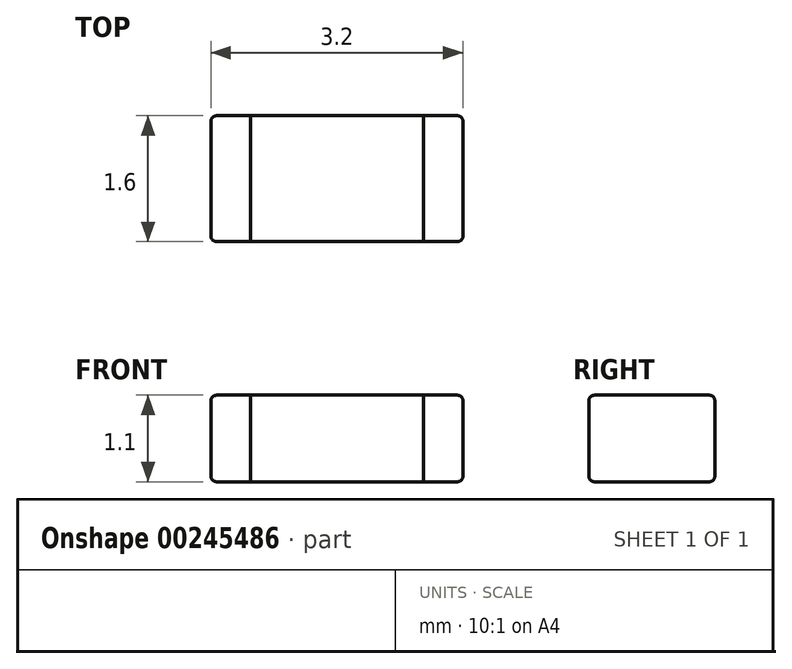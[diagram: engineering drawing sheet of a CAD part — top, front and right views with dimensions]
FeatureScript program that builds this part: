
annotation { "Feature Type Name" : "Feature", "Feature Type Description" : "" }
export const myFeature = defineFeature(function(context is Context, id is Id, definition is map)
    precondition{}
    {
        {
            var Q0;
            Q0=qCreatedBy(makeId("Top.planeOp"),FACE);
            var sketch = newSketch(context, id + "F0", { "sketchPlane" : qUnion([Q0])});
            skLineSegment(sketch, "E0.bottom", {"start": v(1.6, -0.8) * mm, "end": v(-1.6, -0.8) * mm});
            skLineSegment(sketch, "E0.top", {"start": v(1.6, 0.8) * mm, "end": v(-1.6, 0.8) * mm});
            skLineSegment(sketch, "E0.left", {"start": v(1.6, -0.8) * mm, "end": v(1.6, 0.8) * mm});
            skLineSegment(sketch, "E0.right", {"start": v(-1.6, -0.8) * mm, "end": v(-1.6, 0.8) * mm});
            skPoint(sketch, "E0.middle", {"position": v(0, 0) * mm});
            skLineSegment(sketch, "E1", {"start": v(-1.1, 0.8) * mm, "end": v(-1.1, -0.8) * mm});
            skLineSegment(sketch, "E2", {"start": v(1.1, 0.8) * mm, "end": v(1.1, -0.8) * mm});
            skSolve(sketch);
        }
        {
            var Q0;
            {var subQ0=sQuery(id+"F0.wireOp",EDGE,"E0.right");Q0=makeQuery(id+"F0.imprint","IMPRINT",FACE,{"disambiguationData":[TD([[makeQuery(id+"F0.imprint","IMPRINT",EDGE,{"derivedFrom":subQ0}),-1.0]])]});}
            var Q1;
            {var subQ0=sQuery(id+"F0.wireOp",EDGE,"E0.left");Q1=makeQuery(id+"F0.imprint","IMPRINT",FACE,{"disambiguationData":[TD([[makeQuery(id+"F0.imprint","IMPRINT",EDGE,{"derivedFrom":subQ0}),1.0]])]});}
            extrude(context, id + "F1", {"entities" : qUnion([Q0, Q1]), "depth" : 1.1 * mm});
        }
        {
            var Q0;
            {var subQ0=sQuery(id+"F0.wireOp",EDGE,"E1");Q0=makeQuery(id+"F0.imprint","IMPRINT",FACE,{"disambiguationData":[TD([[makeQuery(id+"F0.imprint","IMPRINT",EDGE,{"derivedFrom":subQ0}),1.0]])]});}
            extrude(context, id + "F2", {"entities" : qUnion([Q0]), "depth" : 1.1 * mm});
        }
        {
            var Q0;
            Q0=makeQuery(id+"F1.opExtrude","SWEPT_FACE",FACE,{"disambiguationData":[OSD([sQuery(id+"F0.wireOp",EDGE,"E0.left")])]});
            var Q1;
            Q1=makeQuery(id+"F1.opExtrude","SWEPT_FACE",FACE,{"disambiguationData":[OSD([sQuery(id+"F0.wireOp",EDGE,"E0.right")])]});
            fillet(context, id + "F3", {"entities" : qUnion([Q0, Q1]), "radius" : 0.07 * mm, "tangentPropagation" : true, "allowEdgeOverflow" : false});
        }
        {
            var Q0;
            {var subQ0=sQuery(id+"F0.wireOp",EDGE,"E0.top");Q0=makeQuery(id+"F1.opExtrude","CAP_EDGE",EDGE,{"disambiguationData":[OSD([subQ0]),TDD([makeQuery(id+"F0.imprint","IMPRINT",EDGE,{"disambiguationData":[TD([[makeQuery(id+"F0.imprint","INTERSECT",VERTEX,{"derivedFrom":[subQ0,sQuery(id+"F0.wireOp",EDGE,"E0.left")]}),-1.0]])],"derivedFrom":subQ0})])],"isStart":false});}
            var Q1;
            Q1=makeQuery(id+"F2.opExtrude","CAP_EDGE",EDGE,{"disambiguationData":[OSD([sQuery(id+"F0.wireOp",EDGE,"E0.top")])],"isStart":false});
            var Q2;
            {var subQ0=sQuery(id+"F0.wireOp",EDGE,"E0.top");Q2=makeQuery(id+"F1.opExtrude","CAP_EDGE",EDGE,{"disambiguationData":[OSD([subQ0]),TDD([makeQuery(id+"F0.imprint","IMPRINT",EDGE,{"disambiguationData":[TD([[makeQuery(id+"F0.imprint","INTERSECT",VERTEX,{"derivedFrom":[subQ0,sQuery(id+"F0.wireOp",EDGE,"E0.right")]}),1.0]])],"derivedFrom":subQ0})])],"isStart":false});}
            var Q3;
            Q3=makeQuery(id+"F2.opExtrude","CAP_EDGE",EDGE,{"disambiguationData":[OSD([sQuery(id+"F0.wireOp",EDGE,"E0.top")])],"isStart":true});
            var Q4;
            {var subQ0=sQuery(id+"F0.wireOp",EDGE,"E0.top");Q4=makeQuery(id+"F1.opExtrude","CAP_EDGE",EDGE,{"disambiguationData":[OSD([subQ0]),TDD([makeQuery(id+"F0.imprint","IMPRINT",EDGE,{"disambiguationData":[TD([[makeQuery(id+"F0.imprint","INTERSECT",VERTEX,{"derivedFrom":[subQ0,sQuery(id+"F0.wireOp",EDGE,"E0.right")]}),1.0]])],"derivedFrom":subQ0})])],"isStart":true});}
            var Q5;
            {var subQ0=sQuery(id+"F0.wireOp",EDGE,"E0.top");Q5=makeQuery(id+"F1.opExtrude","CAP_EDGE",EDGE,{"disambiguationData":[OSD([subQ0]),TDD([makeQuery(id+"F0.imprint","IMPRINT",EDGE,{"disambiguationData":[TD([[makeQuery(id+"F0.imprint","INTERSECT",VERTEX,{"derivedFrom":[subQ0,sQuery(id+"F0.wireOp",EDGE,"E0.left")]}),-1.0]])],"derivedFrom":subQ0})])],"isStart":true});}
            var Q6;
            {var subQ0=sQuery(id+"F0.wireOp",EDGE,"E0.bottom");Q6=makeQuery(id+"F1.opExtrude","CAP_EDGE",EDGE,{"disambiguationData":[OSD([subQ0]),TDD([makeQuery(id+"F0.imprint","IMPRINT",EDGE,{"disambiguationData":[TD([[makeQuery(id+"F0.imprint","INTERSECT",VERTEX,{"derivedFrom":[subQ0,sQuery(id+"F0.wireOp",EDGE,"E0.left")]}),-1.0]])],"derivedFrom":subQ0})])],"isStart":false});}
            var Q7;
            Q7=makeQuery(id+"F2.opExtrude","CAP_EDGE",EDGE,{"disambiguationData":[OSD([sQuery(id+"F0.wireOp",EDGE,"E0.bottom")])],"isStart":false});
            var Q8;
            {var subQ0=sQuery(id+"F0.wireOp",EDGE,"E0.bottom");Q8=makeQuery(id+"F1.opExtrude","CAP_EDGE",EDGE,{"disambiguationData":[OSD([subQ0]),TDD([makeQuery(id+"F0.imprint","IMPRINT",EDGE,{"disambiguationData":[TD([[makeQuery(id+"F0.imprint","INTERSECT",VERTEX,{"derivedFrom":[subQ0,sQuery(id+"F0.wireOp",EDGE,"E0.right")]}),1.0]])],"derivedFrom":subQ0})])],"isStart":false});}
            var Q9;
            {var subQ0=sQuery(id+"F0.wireOp",EDGE,"E0.bottom");Q9=makeQuery(id+"F1.opExtrude","CAP_EDGE",EDGE,{"disambiguationData":[OSD([subQ0]),TDD([makeQuery(id+"F0.imprint","IMPRINT",EDGE,{"disambiguationData":[TD([[makeQuery(id+"F0.imprint","INTERSECT",VERTEX,{"derivedFrom":[subQ0,sQuery(id+"F0.wireOp",EDGE,"E0.right")]}),1.0]])],"derivedFrom":subQ0})])],"isStart":true});}
            var Q10;
            Q10=makeQuery(id+"F2.opExtrude","CAP_EDGE",EDGE,{"disambiguationData":[OSD([sQuery(id+"F0.wireOp",EDGE,"E0.bottom")])],"isStart":true});
            var Q11;
            {var subQ0=sQuery(id+"F0.wireOp",EDGE,"E0.bottom");Q11=makeQuery(id+"F1.opExtrude","CAP_EDGE",EDGE,{"disambiguationData":[OSD([subQ0]),TDD([makeQuery(id+"F0.imprint","IMPRINT",EDGE,{"disambiguationData":[TD([[makeQuery(id+"F0.imprint","INTERSECT",VERTEX,{"derivedFrom":[subQ0,sQuery(id+"F0.wireOp",EDGE,"E0.left")]}),-1.0]])],"derivedFrom":subQ0})])],"isStart":true});}
            fillet(context, id + "F4", {"entities" : qUnion([Q0, Q1, Q2, Q3, Q4, Q5, Q6, Q7, Q8, Q9, Q10, Q11]), "radius" : 0.07 * mm, "tangentPropagation" : true, "allowEdgeOverflow" : false});
        }
    });
